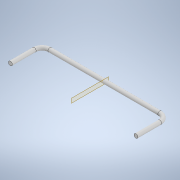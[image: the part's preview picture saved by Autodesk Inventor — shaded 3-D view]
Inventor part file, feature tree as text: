
AUTODESK INVENTOR PART (.ipt)
format: ipt  version: 2022 (Build 260153000, 153)  size: 111,616 bytes
history: native  units: in
note: dims shown in document units (in); Inventor stores cm internally (conversion verified against a paired STEP export)
features: sketch x2, other x1, sweep x1
ambient origin geometry x8: Origin, YZ Plane, XZ Plane, XY Plane, X Axis, Y Axis, Z Axis, Center Point
bodies: Body1 (feature_tree)
feature tree (4):
  other  "ソリッド1"
  sweep  "スイープ1"
  sketch  "スケッチ1"
  sketch  "スケッチ2"
